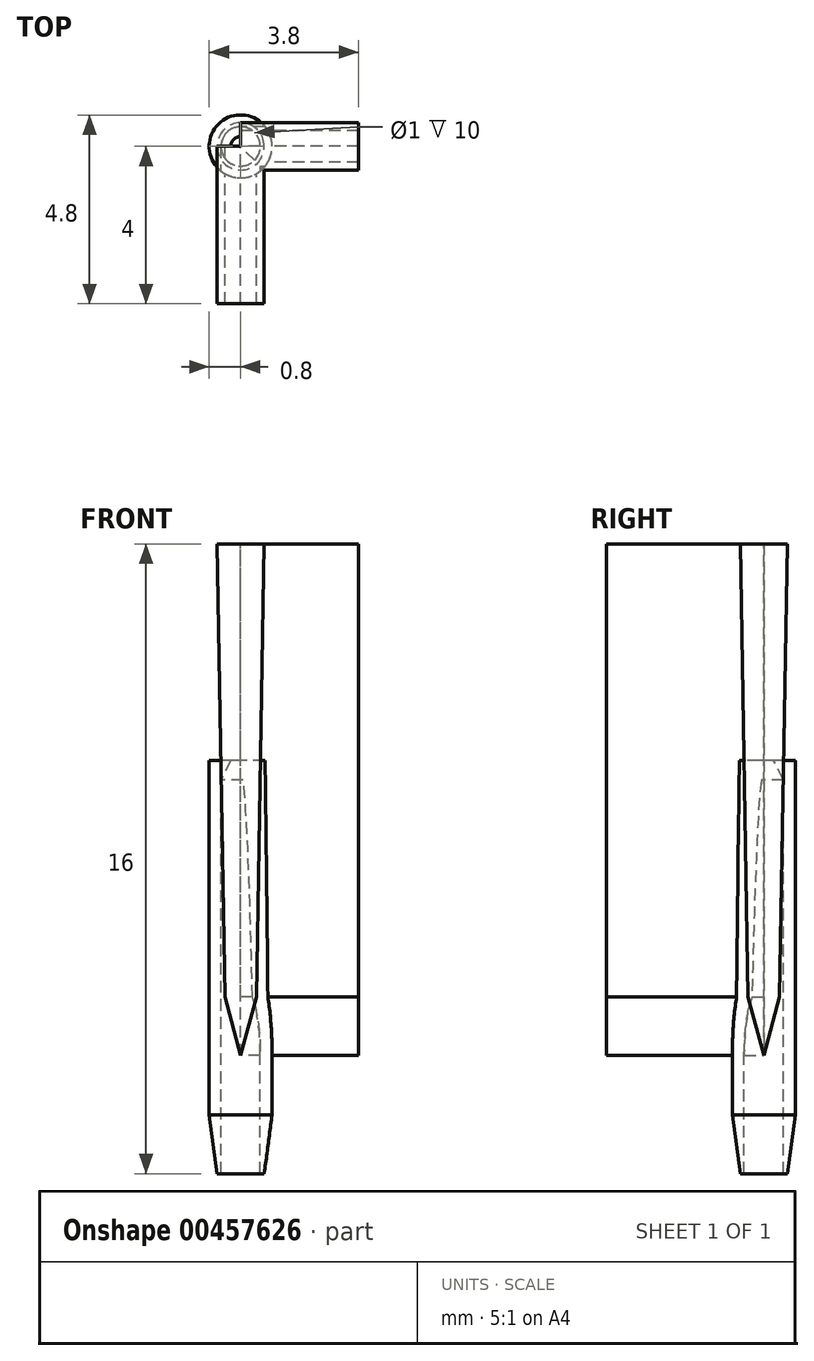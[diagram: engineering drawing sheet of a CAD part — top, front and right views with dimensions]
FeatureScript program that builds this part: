
annotation { "Feature Type Name" : "Feature", "Feature Type Description" : "" }
export const myFeature = defineFeature(function(context is Context, id is Id, definition is map)
    precondition{}
    {
        {
            var Q0;
            Q0=qCreatedBy(makeId("Front.planeOp"),FACE);
            var sketch = newSketch(context, id + "F0", { "sketchPlane" : qUnion([Q0])});
            skLineSegment(sketch, "E0.bottom", {"start": v(-0.8, 10.5) * mm, "end": v(-0.25, 10.5) * mm});
            skLineSegment(sketch, "E0.top", {"start": v(-0.6, 0) * mm, "end": v(-0.5, 0) * mm});
            skLineSegment(sketch, "E0.left", {"start": v(-0.8, 10.5) * mm, "end": v(-0.8, 1.5) * mm});
            skLineSegment(sketch, "E1", {"start": v(-0.8, 1.5) * mm, "end": v(-0.6, 0) * mm});
            skLineSegment(sketch, "E2", {"start": v(-0.8, 1.5) * mm, "end": v(0, 1.5) * mm, "construction": true});
            skPoint(sketch, "E3.orphan", {"position": v(-0.8, 0) * mm});
            skLineSegment(sketch, "E4", {"start": v(0, 12.87) * mm, "end": v(0, 10.5) * mm, "construction": true});
            skLineSegment(sketch, "E5", {"start": v(0, 10.5) * mm, "end": v(0, 0) * mm});
            skLineSegment(sketch, "E6", {"start": v(0, 1.5) * mm, "end": v(0, 0) * mm});
            skLineSegment(sketch, "E7.trimOffspring", {"start": v(0, 1.5) * mm, "end": v(0, -16.93) * mm, "construction": true});
            skLineSegment(sketch, "E8", {"start": v(-0.5, 0) * mm, "end": v(-0.5, 10) * mm});
            skLineSegment(sketch, "E9", {"start": v(-0.5, 10) * mm, "end": v(-0.25, 10.5) * mm});
            skSolve(sketch);
        }
        {
            var Q0;
            Q0=makeQuery(id+"F0.imprint","IMPRINT",FACE,{"disambiguationData":[TD([[makeQuery(id+"F0.imprint","IMPRINT",EDGE,{"derivedFrom":sQuery(id+"F0.wireOp",EDGE,"E0.bottom")}),-1.0]])]});
            var Q1;
            Q1=sQuery(id+"F0.wireOp",EDGE,"E5");
            revolve(context, id + "F1", {"entities" : qUnion([Q0]), "axis" : qUnion([Q1]), "revolveType" : RevolveType.FULL});
        }
        {
            var Q0;
            Q0=qCreatedBy(makeId("Front.planeOp"),FACE);
            var sketch = newSketch(context, id + "F2", { "sketchPlane" : qUnion([Q0])});
            skLineSegment(sketch, "E10", {"start": v(-0.6, 16) * mm, "end": v(-0.4, 4.5) * mm});
            skLineSegment(sketch, "E11", {"start": v(-0.4, 4.5) * mm, "end": v(0, 3) * mm});
            skLineSegment(sketch, "E12", {"start": v(0, 3) * mm, "end": v(0.4, 4.5) * mm});
            skLineSegment(sketch, "E13", {"start": v(0.4, 4.5) * mm, "end": v(0.6, 16) * mm});
            skLineSegment(sketch, "E14", {"start": v(0.6, 16) * mm, "end": v(-0.6, 16) * mm});
            skLineSegment(sketch, "E15", {"start": v(-0.4, 4.5) * mm, "end": v(0.4, 4.5) * mm, "construction": true});
            skSolve(sketch);
        }
        {
            var Q0;
            Q0 = qSketchRegion(id + "F2", true);
            extrude(context, id + "F3", {"entities" : qUnion([Q0]), "operationType" : NewBodyOperationType.ADD, "depth" : 4 * mm, "offsetDistance" : 25 * mm});
        }
        {
            var Q0;
            Q0=qCreatedBy(makeId("Right.planeOp"),FACE);
            var sketch = newSketch(context, id + "F4", { "sketchPlane" : qUnion([Q0])});
            skLineSegment(sketch, "E16", {"start": v(-0.6, 16) * mm, "end": v(-0.4, 4.5) * mm});
            skLineSegment(sketch, "E17", {"start": v(-0.4, 4.5) * mm, "end": v(0, 3) * mm});
            skLineSegment(sketch, "E18", {"start": v(0, 3) * mm, "end": v(0.4, 4.5) * mm});
            skLineSegment(sketch, "E19", {"start": v(0.4, 4.5) * mm, "end": v(0.6, 16) * mm});
            skLineSegment(sketch, "E20", {"start": v(0.6, 16) * mm, "end": v(-0.6, 16) * mm});
            skLineSegment(sketch, "E21", {"start": v(-0.4, 4.5) * mm, "end": v(0.4, 4.5) * mm, "construction": true});
            skSolve(sketch);
        }
        {
            var Q0;
            Q0 = qSketchRegion(id + "F4", true);
            extrude(context, id + "F5", {"entities" : qUnion([Q0]), "operationType" : NewBodyOperationType.ADD, "depth" : 3 * mm, "offsetDistance" : 25 * mm});
        }
    });
